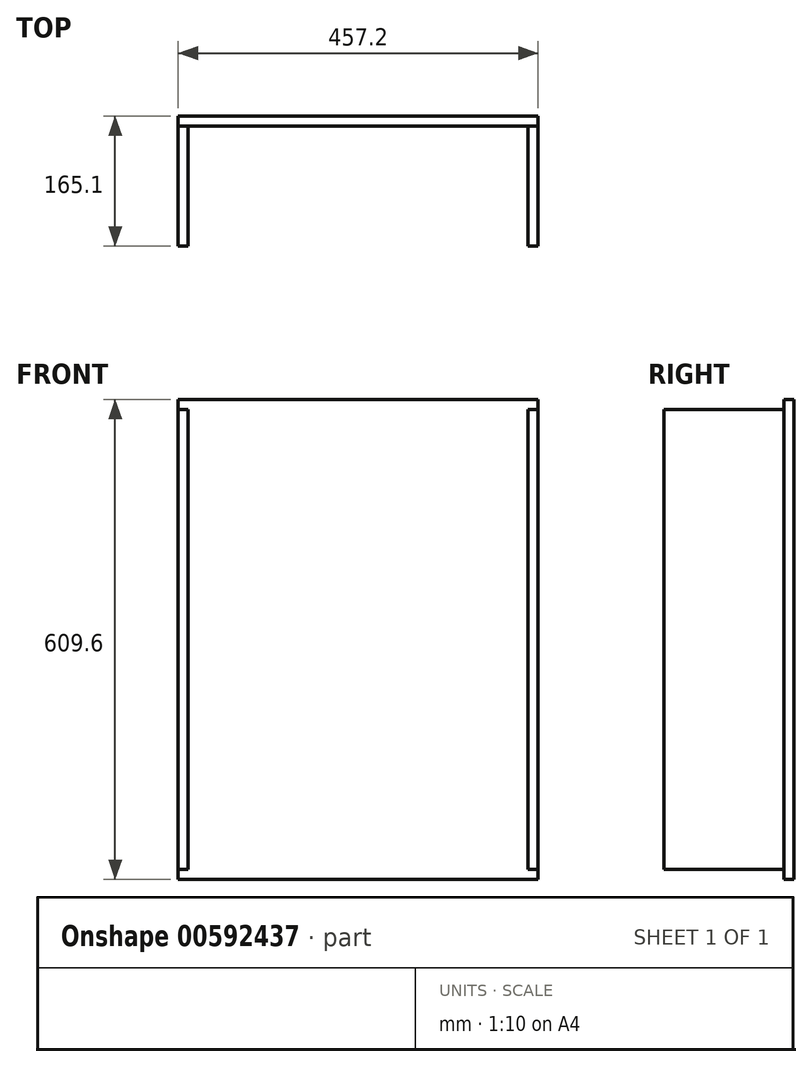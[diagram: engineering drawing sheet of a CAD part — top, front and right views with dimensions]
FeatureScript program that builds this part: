
annotation { "Feature Type Name" : "Feature", "Feature Type Description" : "" }
export const myFeature = defineFeature(function(context is Context, id is Id, definition is map)
    precondition{}
    {
        {
            var Q0;
            Q0=qCreatedBy(makeId("Front.planeOp"),FACE);
            var sketch = newSketch(context, id + "F0", { "sketchPlane" : qUnion([Q0])});
            skLineSegment(sketch, "E0.bottom", {"start": v(-228.6, 304.8) * mm, "end": v(228.6, 304.8) * mm});
            skLineSegment(sketch, "E0.top", {"start": v(-228.6, -304.8) * mm, "end": v(228.6, -304.8) * mm});
            skLineSegment(sketch, "E0.left", {"start": v(-228.6, 304.8) * mm, "end": v(-228.6, -304.8) * mm});
            skLineSegment(sketch, "E0.right", {"start": v(228.6, 304.8) * mm, "end": v(228.6, -304.8) * mm});
            skPoint(sketch, "E0.middle", {"position": v(0, 0) * mm});
            skSolve(sketch);
        }
        {
            var Q0;
            Q0 = qSketchRegion(id + "F0", true);
            extrude(context, id + "F1", {"entities" : qUnion([Q0]), "depth" : 12.7 * mm, "offsetDistance" : 25.4 * mm});
        }
        {
            var Q0;
            Q0=makeQuery(id+"F1.opExtrude","CAP_FACE",FACE,{"disambiguationData":[OSD([sQuery(id+"F0.wireOp",EDGE,"E0.bottom"),sQuery(id+"F0.wireOp",EDGE,"E0.top"),sQuery(id+"F0.wireOp",EDGE,"E0.left"),sQuery(id+"F0.wireOp",EDGE,"E0.right")])],"isStart":false});
            var sketch = newSketch(context, id + "F2", { "sketchPlane" : qUnion([Q0])});
            skLineSegment(sketch, "E1", {"start": v(0, 347.61) * mm, "end": v(0, -392.94) * mm, "construction": true});
            skLineSegment(sketch, "E2.bottom", {"start": v(-228.6, 292.1) * mm, "end": v(-215.9, 292.1) * mm});
            skLineSegment(sketch, "E2.top", {"start": v(-228.6, -292.1) * mm, "end": v(-215.9, -292.1) * mm});
            skLineSegment(sketch, "E2.left", {"start": v(-228.6, 292.1) * mm, "end": v(-228.6, -292.1) * mm});
            skLineSegment(sketch, "E2.right", {"start": v(-215.9, 292.1) * mm, "end": v(-215.9, -292.1) * mm});
            skLineSegment(sketch, "E3", {"start": v(282.18, 0) * mm, "end": v(-299.14, 0) * mm, "construction": true});
            skPoint(sketch, "E3.startSnap0", {"position": v(228.6, 0) * mm});
            skLineSegment(sketch, "E4.MirrorCS", {"start": v(228.6, -292.1) * mm, "end": v(215.9, -292.1) * mm});
            skLineSegment(sketch, "E5.MirrorCS", {"start": v(228.6, 292.1) * mm, "end": v(215.9, 292.1) * mm});
            skLineSegment(sketch, "E6.MirrorCS", {"start": v(215.9, 292.1) * mm, "end": v(215.9, -292.1) * mm});
            skLineSegment(sketch, "E7.MirrorCS", {"start": v(228.6, 292.1) * mm, "end": v(228.6, -292.1) * mm});
            skSolve(sketch);
        }
        {
            var Q0;
            Q0 = qSketchRegion(id + "F2", true);
            extrude(context, id + "F3", {"entities" : qUnion([Q0]), "depth" : 152.4 * mm, "offsetDistance" : 25.4 * mm});
        }
    });
